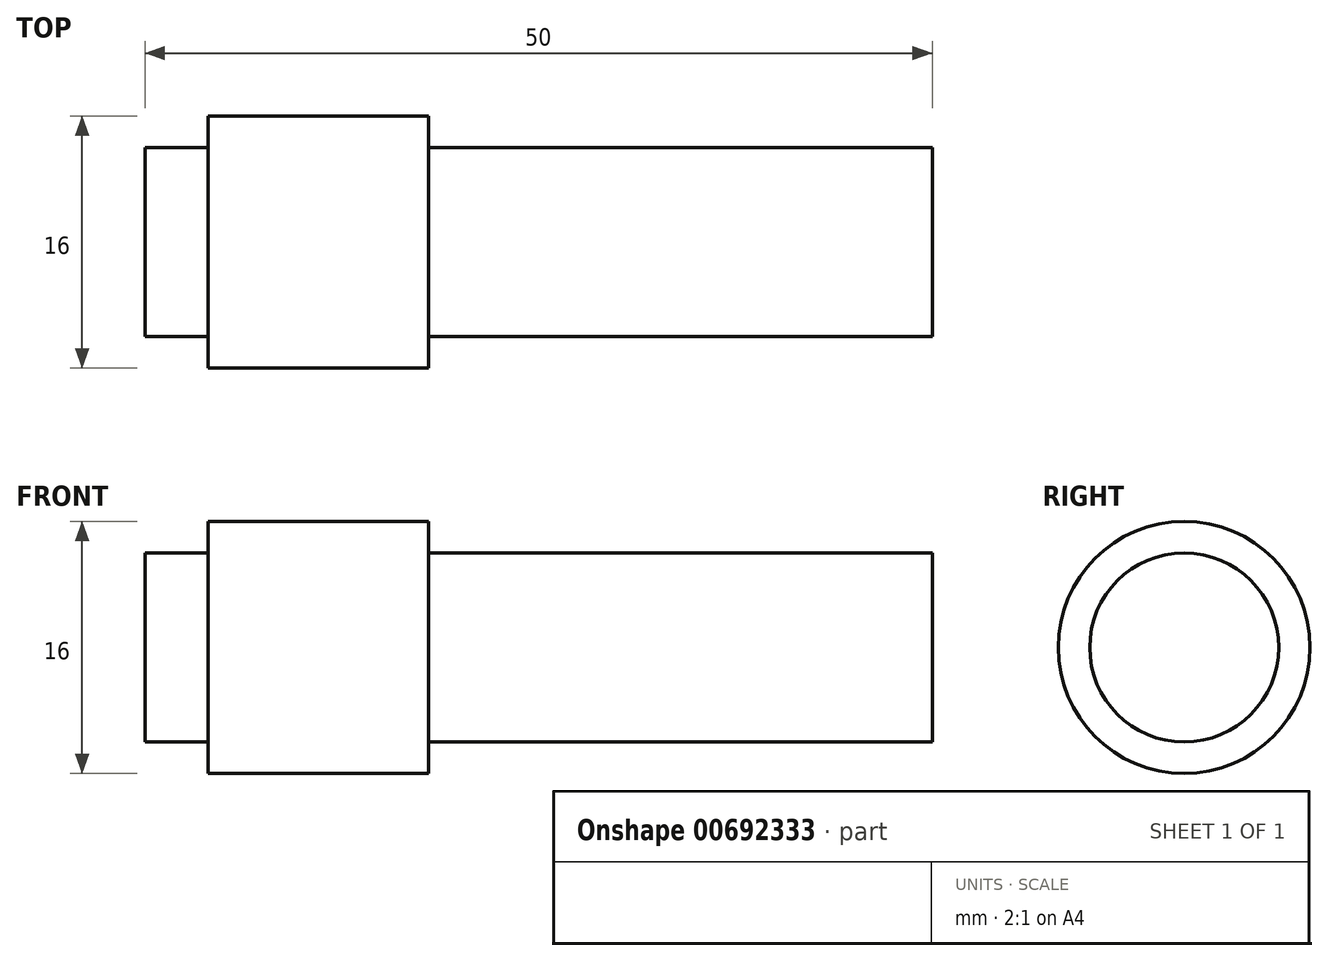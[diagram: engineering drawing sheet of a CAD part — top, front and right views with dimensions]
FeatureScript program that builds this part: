
annotation { "Feature Type Name" : "Feature", "Feature Type Description" : "" }
export const myFeature = defineFeature(function(context is Context, id is Id, definition is map)
    precondition{}
    {
        {
            var Q0;
            Q0=qCreatedBy(makeId("Front.planeOp"),FACE);
            var sketch = newSketch(context, id + "F0", { "sketchPlane" : qUnion([Q0])});
            skLineSegment(sketch, "E0", {"start": v(0, 0) * mm, "end": v(-50, 0) * mm});
            skLineSegment(sketch, "E1", {"start": v(-50, 0) * mm, "end": v(-50, 6) * mm});
            skLineSegment(sketch, "E2", {"start": v(-50, 6) * mm, "end": v(-46, 6) * mm});
            skLineSegment(sketch, "E3", {"start": v(-46, 6) * mm, "end": v(-46, 8) * mm});
            skLineSegment(sketch, "E4", {"start": v(-46, 8) * mm, "end": v(-32, 8) * mm});
            skLineSegment(sketch, "E5", {"start": v(-32, 8) * mm, "end": v(-32, 6) * mm});
            skLineSegment(sketch, "E6", {"start": v(-32, 6) * mm, "end": v(0, 6) * mm});
            skLineSegment(sketch, "E7", {"start": v(0, 6) * mm, "end": v(0, 0) * mm});
            skSolve(sketch);
        }
        {
            var Q0;
            Q0=makeQuery(id+"F0.imprint","IMPRINT",FACE,{"disambiguationData":[TD([[makeQuery(id+"F0.imprint","IMPRINT",EDGE,{"derivedFrom":sQuery(id+"F0.wireOp",EDGE,"E0")}),-1.0]])]});
            var Q1;
            Q1=sQuery(id+"F0.wireOp",EDGE,"E0");
            revolve(context, id + "F1", {"entities" : qUnion([Q0]), "axis" : qUnion([Q1]), "revolveType" : RevolveType.FULL});
        }
    });
